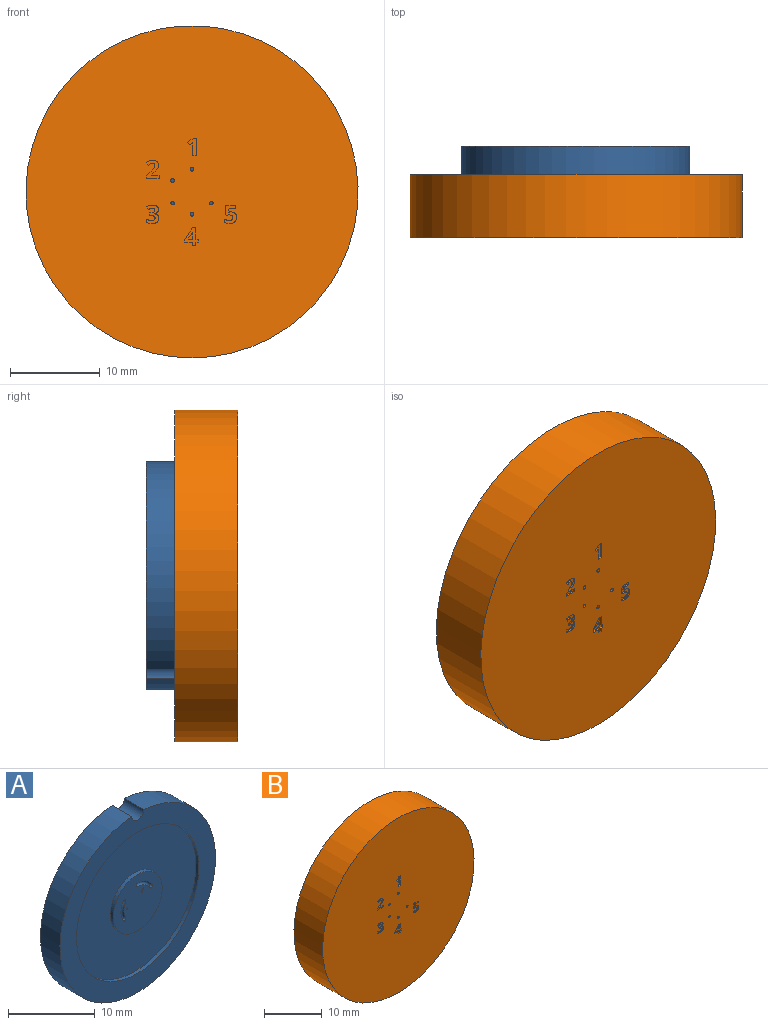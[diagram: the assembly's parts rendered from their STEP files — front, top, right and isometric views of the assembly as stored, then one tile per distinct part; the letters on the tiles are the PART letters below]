
ASSEMBLY  parts=2 mates=1
PART A: 20 faces, bbox 25.4x3.4x25.4 mm
  f0: plane 25.4x25.36mm, normal (0,1,0), area 505.2mm2, adj f1,f19
  f1: cylinder r=12.7mm len=25.4mm, axis (0,-1,0), area 247mm2, adj f0,f2,f19
  f2: plane 25.4x25.36mm, normal (0,-1,0), area 191mm2, adj f1,f17,f19
  f3: plane 8x8mm, normal (0,-1,0), area 47.1mm2, adj f4,f6,f8,f10,f11,f12,f13,f14
  f4: cylinder r=0.12mm len=0.25mm, axis (0,-1,0), area 0.2mm2, adj f3,f5
  f5: plane 0.25x0.25mm, normal (0,-1,0), area 0mm2, adj f4
  f6: cylinder r=0.12mm len=0.25mm, axis (0,-1,0), area 0.2mm2, adj f3,f7
  f7: plane 0.25x0.25mm, normal (0,-1,0), area 0mm2, adj f6
  f8: cylinder r=0.12mm len=0.25mm, axis (0,-1,0), area 0.2mm2, adj f3,f9
  f9: plane 0.25x0.25mm, normal (0,-1,0), area 0mm2, adj f8
  f10: torus R=2.5mm, axis (0,-1,0), area 2.1mm2, adj f3,f11,f12
  f11: sphere r=0.25mm, area 0.2mm2, adj f3,f10
  f12: sphere r=0.25mm, area 0.2mm2, adj f3,f10
  f13: sphere r=0.25mm, area 0.2mm2, adj f3,f14
  f14: torus R=2.5mm, axis (0,-1,0), area 2.1mm2, adj f3,f13,f15
  f15: sphere r=0.25mm, area 0.2mm2, adj f3,f14
  f16: cylinder r=4mm len=8mm, axis (0,-1,0), area 12.6mm2, adj f3,f18
  f17: cylinder r=10mm len=20mm, axis (0,-1,0), area 31.4mm2, adj f2,f18
  f18: plane 20x20mm, normal (0,-1,0), area 263.9mm2, adj f16,f17
  f19: cylinder r=1mm len=3.18mm, axis (0,-1,0), area 9.7mm2, adj f0,f1,f2
PART B: 113 faces, bbox 37x7x37 mm
  f0: plane 37x37mm, normal (0,-1,0), area 1067.4mm2, adj f1,f3,f4,f5,f6,f7,f14,f15
  f1: cylinder r=18.5mm len=37mm, axis (0,1,0), area 813.7mm2, adj f0,f2
  f2: plane 37x37mm, normal (0,1,0), area 1074.6mm2, adj f1,f3,f4,f5,f6,f7
  f3: cylinder r=0.2mm len=7mm, axis (0,1,0), area 8.8mm2, adj f0,f2
  f4: cylinder r=0.2mm len=7mm, axis (0,1,0), area 8.8mm2, adj f0,f2
  f5: cylinder r=0.2mm len=7mm, axis (0,1,0), area 8.8mm2, adj f0,f2
  f6: cylinder r=0.2mm len=7mm, axis (0,1,0), area 8.8mm2, adj f0,f2
  f7: cylinder r=0.2mm len=7mm, axis (0,1,0), area 8.8mm2, adj f0,f2
  f8: plane 0.34x0.2mm, normal (1,0,0), area 0.1mm2, adj f9,f25,f26,f112
  f9: plane 0.48x0.2mm, normal (0,0,-1), area 0.1mm2, adj f8,f10,f26,f112
  f10: plane 0.55x0.36mm, normal (-0.83,0,0.55), area 0.1mm2, adj f9,f11,f26,f112
  f11: extruded ~0.22x0.2mm, area 0mm2, adj f10,f12,f26,f112
  f12: plane 0.2x0.01mm, normal (0,0,1), area 0mm2, adj f11,f13,f26,f112
  f13: extruded ~0.2x0.19mm, area 0mm2, adj f12,f25,f26,f112
  f14: plane 0.24x0.2mm, normal (0,0,1), area 0mm2, adj f0,f15,f24,f26
  f15: plane 0.33x0.2mm, normal (-1,0,0), area 0.1mm2, adj f0,f14,f16,f26
  f16: plane 0.24x0.2mm, normal (0,0,-1), area 0mm2, adj f0,f15,f17,f26
  f17: plane 1.25x0.2mm, normal (-1,0,0), area 0.2mm2, adj f0,f16,f18,f26
  f18: plane 0.39x0.2mm, normal (0,0,-1), area 0.1mm2, adj f0,f17,f19,f26
  f19: plane 1.28x0.87mm, normal (0.83,0,-0.56), area 0.3mm2, adj f0,f18,f20,f26
  f20: plane 0.29x0.2mm, normal (1,0,0), area 0.1mm2, adj f0,f19,f21,f26
  f21: plane 0.85x0.2mm, normal (0,0,1), area 0.2mm2, adj f0,f20,f22,f26
  f22: plane 0.41x0.2mm, normal (1,0,0), area 0.1mm2, adj f0,f21,f23,f26
  f23: plane 0.41x0.2mm, normal (0,0,1), area 0.1mm2, adj f0,f22,f24,f26
  f24: plane 0.41x0.2mm, normal (-1,0,0), area 0.1mm2, adj f0,f14,f23,f26
  f25: extruded ~0.24x0.2mm, area 0mm2, adj f8,f13,f26,f112
  f26: plane 1.98x1.49mm, normal (0,-1,0), area 1.5mm2, adj f8,f9,f10,f11,f12,f13,f14,f15
  f27: extruded ~0.46x0.2mm, area 0.1mm2, adj f0,f28,f46,f47
  f28: extruded ~0.21x0.2mm, area 0mm2, adj f0,f27,f29,f47
  f29: plane 0.2x0.05mm, normal (0.2,0,-0.98), area 0mm2, adj f0,f28,f30,f47
  f30: plane 0.39x0.2mm, normal (-1,0,0.09), area 0.1mm2, adj f0,f29,f31,f47
  f31: plane 0.71x0.2mm, normal (0,0,1), area 0.1mm2, adj f0,f30,f32,f47
  f32: plane 0.36x0.2mm, normal (-1,0,0), area 0.1mm2, adj f0,f31,f33,f47
  f33: plane 1.08x0.2mm, normal (0,0,-1), area 0.2mm2, adj f0,f32,f34,f47
  f34: plane 1.01x0.2mm, normal (1,0,-0.07), area 0.2mm2, adj f0,f33,f35,f47
  f35: plane 0.2x0.17mm, normal (0.47,0,0.88), area 0mm2, adj f0,f34,f36,f47
  f36: extruded ~0.2x0.14mm, area 0mm2, adj f0,f35,f37,f47
  f37: extruded ~0.2x0.16mm, area 0mm2, adj f0,f36,f38,f47
  f38: extruded ~0.4x0.3mm, area 0.1mm2, adj f0,f37,f39,f47
  f39: extruded ~0.38x0.31mm, area 0.1mm2, adj f0,f38,f40,f47
  f40: extruded ~0.27x0.2mm, area 0.1mm2, adj f0,f39,f41,f47
  f41: extruded ~0.25x0.2mm, area 0.1mm2, adj f0,f40,f42,f47
  f42: plane 0.36x0.2mm, normal (1,0,0), area 0.1mm2, adj f0,f41,f43,f47
  f43: extruded ~0.53x0.2mm, area 0.1mm2, adj f0,f42,f44,f47
  f44: extruded ~0.59x0.2mm, area 0.1mm2, adj f0,f43,f45,f47
  f45: extruded ~0.51x0.21mm, area 0.1mm2, adj f0,f44,f46,f47
  f46: extruded ~0.44x0.2mm, area 0.1mm2, adj f0,f27,f45,f47
  f47: plane 2.01x1.33mm, normal (0,-1,0), area 1.6mm2, adj f27,f28,f29,f30,f31,f32,f33,f34
  f48: extruded ~0.32x0.2mm, area 0.1mm2, adj f0,f49,f74,f75
  f49: extruded ~0.35x0.2mm, area 0.1mm2, adj f0,f48,f50,f75
  f50: extruded ~0.49x0.2mm, area 0.1mm2, adj f0,f49,f51,f75
  f51: extruded ~0.65x0.2mm, area 0.1mm2, adj f0,f50,f52,f75
  f52: plane 0.29x0.2mm, normal (0.83,0,0.56), area 0.1mm2, adj f0,f51,f53,f75
  f53: extruded ~0.22x0.2mm, area 0.1mm2, adj f0,f52,f54,f75
  f54: extruded ~0.2x0.2mm, area 0mm2, adj f0,f53,f55,f75
  f55: extruded ~0.28x0.23mm, area 0.1mm2, adj f0,f54,f56,f75
  f56: extruded ~0.21x0.2mm, area 0mm2, adj f0,f55,f57,f75
  f57: extruded ~0.34x0.2mm, area 0.1mm2, adj f0,f56,f58,f75
  f58: plane 0.2x0.15mm, normal (0,0,-1), area 0mm2, adj f0,f57,f59,f75
  f59: plane 0.32x0.2mm, normal (1,0,0), area 0.1mm2, adj f0,f58,f60,f75
  f60: plane 0.2x0.15mm, normal (0,0,1), area 0mm2, adj f0,f59,f61,f75
  f61: extruded ~0.36x0.2mm, area 0.1mm2, adj f0,f60,f62,f75
  f62: extruded ~0.2x0.2mm, area 0mm2, adj f0,f61,f63,f75
  f63: extruded ~0.23x0.2mm, area 0.1mm2, adj f0,f62,f64,f75
  f64: extruded ~0.31x0.2mm, area 0.1mm2, adj f0,f63,f65,f75
  f65: extruded ~0.27x0.2mm, area 0.1mm2, adj f0,f64,f66,f75
  f66: extruded ~0.25x0.2mm, area 0.1mm2, adj f0,f65,f67,f75
  f67: plane 0.36x0.2mm, normal (1,0,0), area 0.1mm2, adj f0,f66,f68,f75
  f68: extruded ~0.57x0.2mm, area 0.1mm2, adj f0,f67,f69,f75
  f69: extruded ~0.59x0.2mm, area 0.1mm2, adj f0,f68,f70,f75
  f70: extruded ~0.45x0.21mm, area 0.1mm2, adj f0,f69,f71,f75
  f71: extruded ~0.31x0.2mm, area 0.1mm2, adj f0,f70,f72,f75
  f72: extruded ~0.36x0.2mm, area 0.1mm2, adj f0,f71,f73,f75
  f73: plane 0.2x0.01mm, normal (-1,0,0), area 0mm2, adj f0,f72,f74,f75
  f74: extruded ~0.32x0.2mm, area 0.1mm2, adj f0,f48,f73,f75
  f75: plane 2.04x1.37mm, normal (0,-1,0), area 1.5mm2, adj f48,f49,f50,f51,f52,f53,f54,f55
  f76: plane 1.39x0.2mm, normal (0,0,1), area 0.3mm2, adj f0,f77,f99,f100
  f77: plane 0.35x0.2mm, normal (-1,0,0), area 0.1mm2, adj f0,f76,f78,f100
  f78: plane 0.86x0.2mm, normal (0,0,-1), area 0.2mm2, adj f0,f77,f79,f100
  f79: plane 0.2x0.02mm, normal (-1,0,0), area 0mm2, adj f0,f78,f80,f100
  f80: plane 0.26x0.24mm, normal (-0.69,0,0.73), area 0.1mm2, adj f0,f79,f81,f100
  f81: extruded ~0.36x0.36mm, area 0.1mm2, adj f0,f80,f82,f100
  f82: extruded ~0.25x0.2mm, area 0.1mm2, adj f0,f81,f83,f100
  f83: extruded ~0.26x0.2mm, area 0.1mm2, adj f0,f82,f84,f100
  f84: extruded ~0.28x0.2mm, area 0.1mm2, adj f0,f83,f85,f100
  f85: extruded ~0.22x0.2mm, area 0.1mm2, adj f0,f84,f86,f100
  f86: extruded ~0.33x0.2mm, area 0.1mm2, adj f0,f85,f87,f100
  f87: extruded ~0.26x0.2mm, area 0.1mm2, adj f0,f86,f88,f100
  f88: extruded ~0.21x0.2mm, area 0mm2, adj f0,f87,f89,f100
  f89: extruded ~0.24x0.2mm, area 0.1mm2, adj f0,f88,f90,f100
  f90: plane 0.27x0.23mm, normal (0.76,0,0.65), area 0.1mm2, adj f0,f89,f91,f100
  f91: extruded ~0.23x0.2mm, area 0.1mm2, adj f0,f90,f92,f100
  f92: extruded ~0.22x0.2mm, area 0mm2, adj f0,f91,f93,f100
  f93: extruded ~0.2x0.18mm, area 0mm2, adj f0,f92,f94,f100
  f94: extruded ~0.2x0.18mm, area 0mm2, adj f0,f93,f95,f100
  f95: extruded ~0.2x0.15mm, area 0mm2, adj f0,f94,f96,f100
  f96: extruded ~0.2x0.16mm, area 0mm2, adj f0,f95,f97,f100
  f97: extruded ~0.31x0.29mm, area 0.1mm2, adj f0,f96,f98,f100
  f98: plane 0.5x0.5mm, normal (0.71,0,-0.7), area 0.1mm2, adj f0,f97,f99,f100
  f99: plane 0.29x0.2mm, normal (1,0,0), area 0.1mm2, adj f0,f76,f98,f100
  f100: plane 2.01x1.39mm, normal (0,-1,0), area 1.5mm2, adj f76,f77,f78,f79,f80,f81,f82,f83
  f101: plane 0.42x0.2mm, normal (0,0,1), area 0.1mm2, adj f0,f102,f110,f111
  f102: plane 1.98x0.2mm, normal (-1,0,0), area 0.4mm2, adj f0,f101,f103,f111
  f103: plane 0.34x0.2mm, normal (0,0,-1), area 0.1mm2, adj f0,f102,f104,f111
  f104: plane 0.64x0.51mm, normal (0.62,0,-0.78), area 0.2mm2, adj f0,f103,f105,f111
  f105: plane 0.25x0.2mm, normal (0.78,0,0.63), area 0.1mm2, adj f0,f104,f106,f111
  f106: plane 0.23x0.2mm, normal (-0.63,0,0.78), area 0.1mm2, adj f0,f105,f107,f111
  f107: extruded ~0.2x0.15mm, area 0mm2, adj f0,f106,f108,f111
  f108: plane 0.21x0.2mm, normal (1,0,-0.03), area 0mm2, adj f0,f107,f109,f111
  f109: plane 0.2x0.19mm, normal (1,0,-0.02), area 0mm2, adj f0,f108,f110,f111
  f110: plane 1.15x0.2mm, normal (1,0,0), area 0.2mm2, adj f0,f101,f109,f111
  f111: plane 1.98x0.98mm, normal (0,-1,0), area 1mm2, adj f101,f102,f103,f104,f105,f106,f107,f108
  f112: plane 0.77x0.5mm, normal (0,-1,0), area 0.2mm2, adj f8,f9,f10,f11,f12,f13,f25
PLACE A rot(axis=(0,-1,0),150deg) t=(0,0,0)mm
PLACE B at identity fixed
MATE revolute B.f1 <-> A.f16  axis (0,1,0) through (0,0,0)mm
